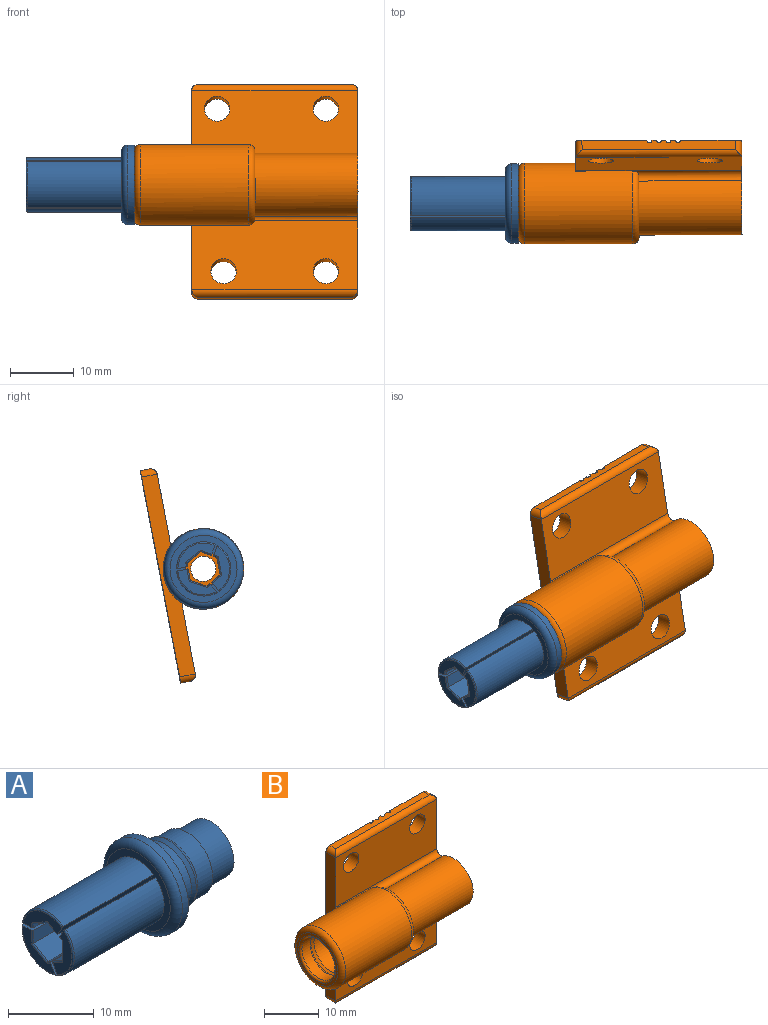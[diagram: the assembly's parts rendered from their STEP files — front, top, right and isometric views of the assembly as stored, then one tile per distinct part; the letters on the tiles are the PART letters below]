
ASSEMBLY  parts=2 mates=1
PART A: 47 faces, bbox 27x13.6x13.6 mm
  f0: plane 6.38x3.23mm, normal (-1,0,0), area 9mm2, adj f31,f34,f37,f38,f39,f46
  f1: cylinder r=4.27mm len=14.8mm, axis (-1,0,0), area 126.3mm2, adj f10,f26,f29,f35
  f2: plane 5.34x4.5mm, normal (-1,0,0), area 9mm2, adj f26,f29,f35,f40,f41,f42
  f3: cylinder r=4.27mm len=14.8mm, axis (-1,0,0), area 126.3mm2, adj f10,f22,f23,f36
  f4: plane 6.75x3.15mm, normal (-1,0,0), area 9mm2, adj f22,f23,f36,f43,f44,f45
  f5: cylinder r=2.77mm len=12mm, axis (-1,0,0), area 4.9mm2, adj f10,f12,f23,f34
  f6: cylinder r=2.77mm len=12mm, axis (-1,0,0), area 4.9mm2, adj f10,f12,f29,f31
  f7: cylinder r=2.77mm len=12mm, axis (-1,0,0), area 4.9mm2, adj f10,f12,f22,f26
  f8: plane 12.54x12.54mm, normal (1,0,0), area 66.2mm2, adj f9,f18
  f9: cylinder r=6.27mm len=12.54mm, axis (-1,0,0), area 39.4mm2, adj f8,f19
  f10: plane 10.54x10.54mm, normal (-1,0,0), area 31.8mm2, adj f1,f3,f5,f6,f7,f11,f19,f22
  f11: cylinder r=4.27mm len=14.8mm, axis (-1,0,0), area 126.3mm2, adj f10,f31,f34,f46
  f12: plane 7.54x7.54mm, normal (1,0,0), area 24.4mm2, adj f5,f6,f7,f13,f20,f21,f22,f23
  f13: cylinder r=3.77mm len=7.54mm, axis (-1,0,0), area 94.7mm2, adj f12,f14
  f14: plane 8.54x8.54mm, normal (1,0,0), area 12.6mm2, adj f13,f15
  f15: cylinder r=4.27mm len=8.54mm, axis (-1,0,0), area 67.1mm2, adj f14,f16
  f16: cone r=4.57mm half-angle=31deg, axis (-1,0,0), area 16.2mm2, adj f15,f17
  f17: cone r=4.27mm half-angle=31deg, axis (1,0,0), area 16.2mm2, adj f16,f18
  f18: cylinder r=4.27mm len=8.54mm, axis (-1,0,0), area 67.1mm2, adj f8,f17
  f19: torus R=5.27mm, axis (1,0,0), area 58.3mm2, adj f9,f10
  f20: plane 26.8x2.77mm, normal (0,1,0), area 74.2mm2, adj f12,f21,f24,f44
  f21: plane 26.8x1.58mm, normal (0,0.5,0.87), area 48.7mm2, adj f12,f20,f22,f45
  f22: plane 27.01x1.61mm, normal (0,0.87,-0.5), area 31.8mm2, adj f3,f4,f7,f10,f12,f21,f36,f45
  f23: plane 27.02x1.57mm, normal (0,0.87,0.5), area 29.7mm2, adj f3,f4,f5,f10,f12,f24,f36,f43
  f24: plane 26.8x0.48mm, normal (0,0.5,-0.87), area 14.7mm2, adj f12,f20,f23,f43
  f25: plane 26.8x2.4mm, normal (0,-0.5,0.87), area 74.2mm2, adj f12,f27,f28,f41
  f26: plane 27.02x1.57mm, normal (0,-0.87,0.5), area 29.7mm2, adj f1,f2,f7,f10,f12,f27,f35,f40
  f27: plane 26.8x0.48mm, normal (0,0.5,0.87), area 14.7mm2, adj f12,f25,f26,f40
  f28: plane 26.8x1.82mm, normal (0,-1,0), area 48.7mm2, adj f12,f25,f29,f42
  f29: plane 27.01x1.86mm, normal (0,0,1), area 31.8mm2, adj f1,f2,f6,f10,f12,f28,f35,f42
  f30: plane 26.8x2.4mm, normal (0,-0.5,-0.87), area 74.2mm2, adj f12,f32,f33,f38
  f31: plane 27.02x1.81mm, normal (0,0,-1), area 29.7mm2, adj f0,f6,f10,f11,f12,f32,f37,f46
  f32: plane 26.8x0.55mm, normal (0,-1,0), area 14.7mm2, adj f12,f30,f31,f37
  f33: plane 26.8x1.58mm, normal (0,0.5,-0.87), area 48.7mm2, adj f12,f30,f34,f39
  f34: plane 27.01x1.61mm, normal (0,-0.87,-0.5), area 31.8mm2, adj f0,f5,f10,f11,f12,f33,f39,f46
  f35: torus R=4.07mm, axis (1,0,0), area 2.6mm2, adj f1,f2,f26,f29
  f36: torus R=4.07mm, axis (1,0,0), area 2.6mm2, adj f3,f4,f22,f23
  f37: cylinder r=0.2mm len=0.67mm, axis (0,0,-1), area 0.2mm2, adj f0,f31,f32,f38
  f38: cylinder r=0.2mm len=2.7mm, axis (0,0.87,-0.5), area 0.9mm2, adj f0,f30,f37,f39
  f39: cylinder r=0.2mm len=1.78mm, axis (0,0.87,0.5), area 0.6mm2, adj f0,f33,f34,f38
  f40: cylinder r=0.2mm len=0.68mm, axis (0,-0.87,0.5), area 0.2mm2, adj f2,f26,f27,f41
  f41: cylinder r=0.2mm len=2.7mm, axis (0,-0.87,-0.5), area 0.9mm2, adj f2,f25,f40,f42
  f42: cylinder r=0.2mm len=1.93mm, axis (0,0,-1), area 0.6mm2, adj f2,f28,f29,f41
  f43: cylinder r=0.2mm len=0.68mm, axis (0,0.87,0.5), area 0.2mm2, adj f4,f23,f24,f44
  f44: cylinder r=0.2mm len=3mm, axis (0,0,1), area 0.9mm2, adj f4,f20,f43,f45
  f45: cylinder r=0.2mm len=1.78mm, axis (0,-0.87,0.5), area 0.6mm2, adj f4,f21,f22,f44
  f46: torus R=4.07mm, axis (1,0,0), area 2.6mm2, adj f0,f11,f31,f34
PART B: 46 faces, bbox 35.2x13.7x34 mm
  f0: cylinder r=2.41mm len=4.82mm, axis (-1,0,0), area 66.2mm2, adj f1,f15
  f1: plane 9.96x9.96mm, normal (1,0,0), area 59.7mm2, adj f0,f2
  f2: cylinder r=4.98mm len=16.2mm, axis (-1,0,0), area 349.7mm2, adj f1,f3,f22,f35,f36
  f3: plane 10.7x8.92mm, normal (1,0,0), area 8.6mm2, adj f2,f33,f35,f36
  f4: cylinder r=6.35mm len=17mm, axis (-1,0,0), area 584.5mm2, adj f16,f33,f34,f35,f36
  f5: plane 10.7x10.7mm, normal (-1,0,0), area 19mm2, adj f34,f45
  f6: cylinder r=4.35mm len=8.7mm, axis (-1,0,0), area 57.4mm2, adj f7,f45
  f7: cone r=4.65mm half-angle=31deg, axis (1,0,0), area 16.5mm2, adj f6,f8
  f8: cone r=4.35mm half-angle=31deg, axis (-1,0,0), area 16.5mm2, adj f7,f9
  f9: cylinder r=4.35mm len=13.5mm, axis (-1,0,0), area 368.9mm2, adj f8,f10
  f10: plane 8.7x8.7mm, normal (-1,0,0), area 47.1mm2, adj f9,f11
  f11: cylinder r=1.98mm len=11.65mm, axis (-1,0,0), area 144.9mm2, adj f10,f12
  f12: cone r=1.98mm half-angle=20deg, axis (1,0,0), area 17.3mm2, adj f11,f13
  f13: cylinder r=2.41mm len=4.82mm, axis (-1,0,0), area 8.3mm2, adj f12,f14
  f14: cone r=2.41mm half-angle=35deg, axis (-1,0,0), area 5.3mm2, adj f13,f15
  f15: cone r=2.2mm half-angle=55deg, axis (1,0,0), area 3.7mm2, adj f0,f14
  f16: plane 32x2.54mm, normal (-1,0,0), area 67.2mm2, adj f4,f17,f18,f21,f29,f31,f35,f36
  f17: plane 26.1x11.05mm, normal (0,-1,0), area 263.2mm2, adj f16,f22,f24,f25,f28,f35
  f18: plane 26.1x11.05mm, normal (0,-1,0), area 263.2mm2, adj f16,f22,f23,f26,f32,f36
  f19: plane 24.1x1.5mm, normal (0,0,1), area 35.1mm2, adj f21,f27,f28,f29,f37,f39,f41,f43
  f20: plane 24.1x1.5mm, normal (0,0,-1), area 36.2mm2, adj f21,f30,f31,f32
  f21: plane 34x26.1mm, normal (0,1,0), area 823.5mm2, adj f16,f19,f20,f22,f23,f24,f25,f26
  f22: plane 32x4.06mm, normal (1,0,0), area 80.1mm2, adj f2,f17,f18,f21,f27,f30,f35,f36
  f23: cylinder r=2mm len=4mm, axis (0,-1,0), area 31.4mm2, adj f18,f21
  f24: cylinder r=2mm len=4mm, axis (0,-1,0), area 31.4mm2, adj f17,f21
  f25: cylinder r=2mm len=4mm, axis (0,-1,0), area 31.4mm2, adj f17,f21
  f26: cylinder r=2mm len=4mm, axis (0,-1,0), area 31.4mm2, adj f18,f21
  f27: cylinder r=1mm len=2.5mm, axis (0,1,0), area 3.4mm2, adj f19,f21,f22,f28
  f28: cylinder r=1mm len=26.1mm, axis (-1,0,0), area 39.9mm2, adj f17,f19,f27,f29
  f29: cylinder r=1mm len=2.5mm, axis (0,-1,0), area 3.4mm2, adj f16,f19,f21,f28
  f30: cylinder r=1mm len=2.5mm, axis (0,-1,0), area 3.4mm2, adj f20,f21,f22,f32
  f31: cylinder r=1mm len=2.5mm, axis (0,1,0), area 3.4mm2, adj f16,f20,f21,f32
  f32: cylinder r=1mm len=26.1mm, axis (1,0,0), area 39.9mm2, adj f18,f20,f30,f31
  f33: torus R=5.35mm, axis (-1,0,0), area 43.7mm2, adj f3,f4,f35,f36
  f34: torus R=5.35mm, axis (-1,0,0), area 59.1mm2, adj f4,f5
  f35: cylinder r=1mm len=26.1mm, axis (-1,0,0), area 38.1mm2, adj f2,f3,f4,f16,f17,f22,f33
  f36: cylinder r=1mm len=26.1mm, axis (-1,0,0), area 38.1mm2, adj f2,f3,f4,f16,f18,f22,f33
  f37: cylinder r=0.4mm len=10mm, axis (0,0,1), area 12.6mm2, adj f19,f21,f38
  f38: plane 0.8x0.4mm, normal (0,0,1), area 0.3mm2, adj f21,f37
  f39: cylinder r=0.4mm len=2mm, axis (0,0,1), area 2.5mm2, adj f19,f21,f40
  f40: plane 0.8x0.4mm, normal (0,0,1), area 0.3mm2, adj f21,f39
  f41: cylinder r=0.4mm len=2mm, axis (0,0,1), area 2.5mm2, adj f19,f21,f42
  f42: plane 0.8x0.4mm, normal (0,0,1), area 0.3mm2, adj f21,f41
  f43: cylinder r=0.4mm len=2mm, axis (0,0,1), area 2.5mm2, adj f19,f21,f44
  f44: plane 0.8x0.4mm, normal (0,0,1), area 0.3mm2, adj f21,f43
  f45: torus R=4.75mm, axis (-1,0,0), area 17.7mm2, adj f5,f6
PLACE A rot(axis=(-1,0,0.01),10.8deg) t=(0.01,133.03,-107.35)mm
PLACE B rot(axis=(-1,0,0.01),10.8deg) t=(30.08,133.09,-107.34)mm
MATE cylindrical A.f1 <-> B.f0  axis (-1,0,0) through (10.96,133.06,-107.35)mm
